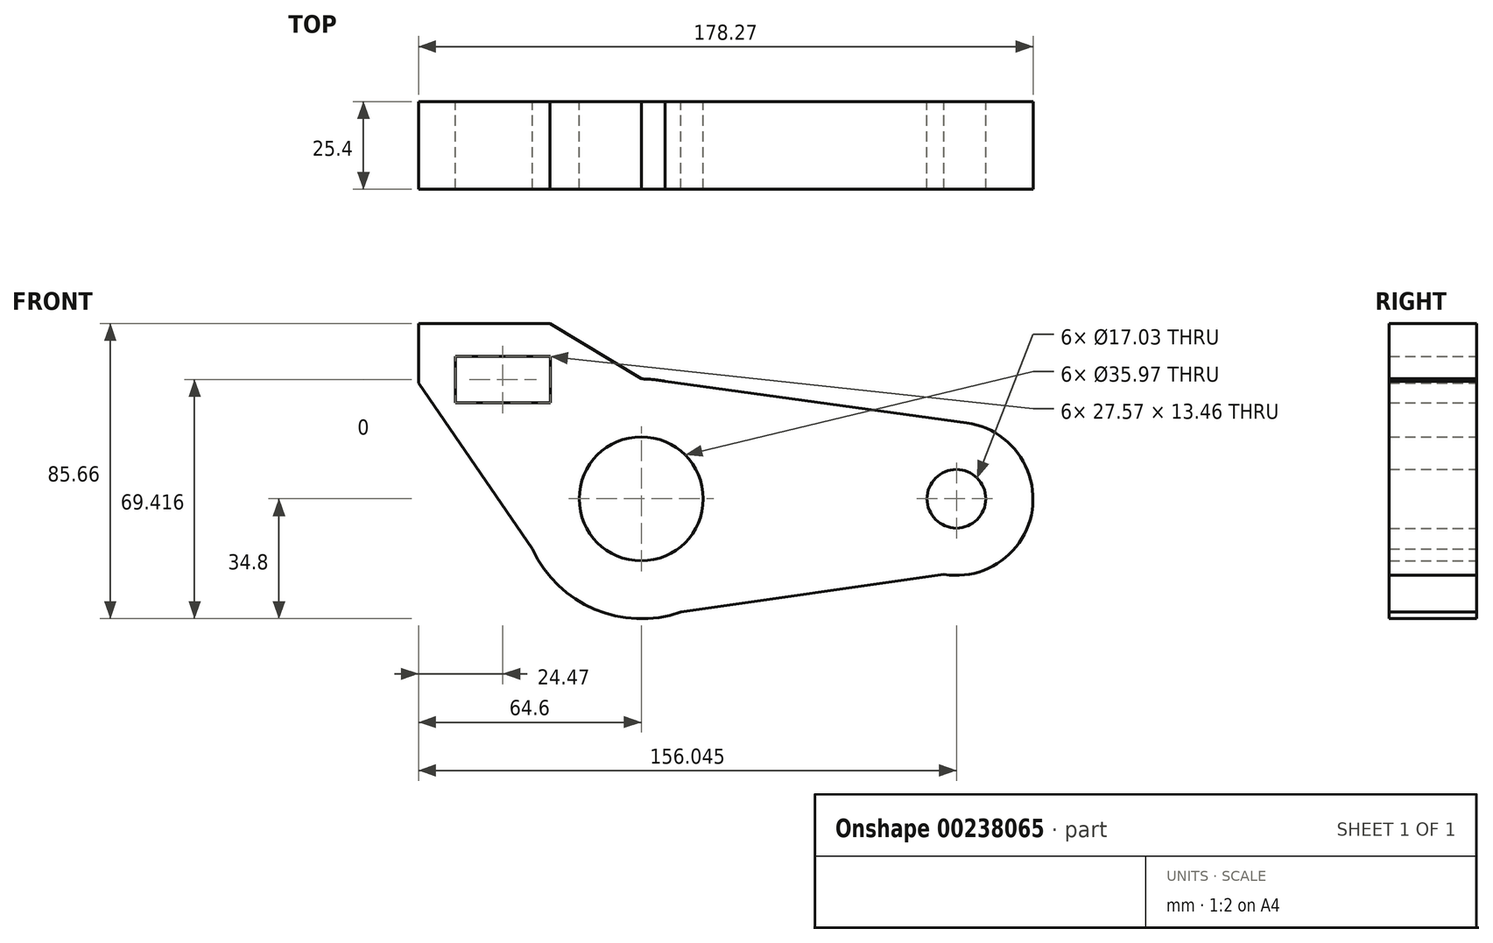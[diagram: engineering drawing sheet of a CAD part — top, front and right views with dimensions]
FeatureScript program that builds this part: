
annotation { "Feature Type Name" : "Feature", "Feature Type Description" : "" }
export const myFeature = defineFeature(function(context is Context, id is Id, definition is map)
    precondition{}
    {
        {
            var Q0;
            Q0=qCreatedBy(makeId("Front.planeOp"),FACE);
            var sketch = newSketch(context, id + "F0", { "sketchPlane" : qUnion([Q0])});
            skCircle(sketch, "E0", {"center": v(0, 0) * mm, "radius": 34.8 * mm});
            skCircle(sketch, "E1", {"center": v(0, 0) * mm, "radius": 17.99 * mm});
            skLineSegment(sketch, "E2.bottom", {"start": v(-64.6, 50.86) * mm, "end": v(-26.5, 50.86) * mm});
            skLineSegment(sketch, "E2.top", {"start": v(-64.6, 33.63) * mm, "end": v(-26.5, 33.63) * mm});
            skLineSegment(sketch, "E2.left", {"start": v(-64.6, 50.86) * mm, "end": v(-64.6, 33.63) * mm});
            skLineSegment(sketch, "E2.right", {"start": v(-26.5, 50.86) * mm, "end": v(-26.5, 33.63) * mm});
            skLineSegment(sketch, "E3", {"start": v(-64.6, 33.63) * mm, "end": v(-31.59, -14.6) * mm});
            skLineSegment(sketch, "E4", {"start": v(-26.5, 50.86) * mm, "end": v(0, 34.8) * mm});
            skCircle(sketch, "E5", {"center": v(91.44, 0) * mm, "radius": 22.23 * mm});
            skLineSegment(sketch, "E6", {"start": v(11.48, -32.85) * mm, "end": v(87.88, -21.94) * mm});
            skLineSegment(sketch, "E7", {"start": v(0, 34.8) * mm, "end": v(-26.5, 34.8) * mm});
            skLineSegment(sketch, "E8", {"start": v(2.52, 34.7) * mm, "end": v(94.48, 22.02) * mm});
            skCircle(sketch, "E9", {"center": v(91.44, 0) * mm, "radius": 8.52 * mm});
            skLineSegment(sketch, "E10.bottom", {"start": v(-53.92, 41.35) * mm, "end": v(-26.34, 41.35) * mm});
            skLineSegment(sketch, "E10.top", {"start": v(-53.92, 27.89) * mm, "end": v(-26.34, 27.89) * mm});
            skLineSegment(sketch, "E10.left", {"start": v(-53.92, 41.35) * mm, "end": v(-53.92, 27.89) * mm});
            skLineSegment(sketch, "E10.right", {"start": v(-26.34, 41.35) * mm, "end": v(-26.34, 27.89) * mm});
            skSolve(sketch);
        }
        {
            var Q0;
            Q0 = qSketchRegion(id + "F0", true);
            extrude(context, id + "F1", {"entities" : qUnion([Q0]), "depth" : 25.4 * mm});
        }
    });
